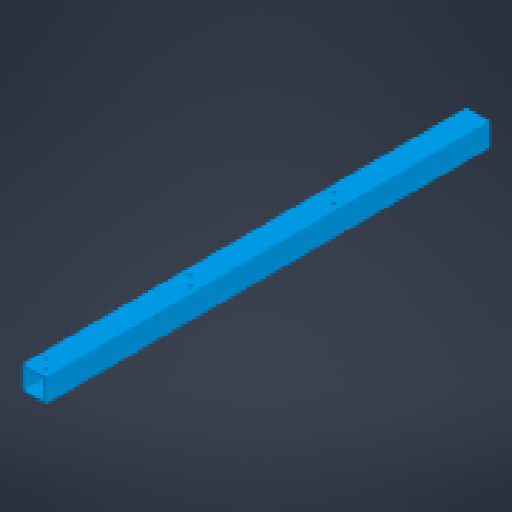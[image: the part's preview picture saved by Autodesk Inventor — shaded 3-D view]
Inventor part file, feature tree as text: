
AUTODESK INVENTOR PART (.ipt)
format: ipt  version: 2024 (Build 280153000, 153)  size: 178,176 bytes
history: native  units: mm
features: extrude x2, sketch x2, other x1
ambient origin geometry x8: Origin, YZ Plane, XZ Plane, XY Plane, X Axis, Y Axis, Z Axis, Center Point
bodies: Body1 (feature_tree)
feature tree (5):
  other  "Твердое тело1"
  extrude  "Выдавливание1"  Depth=380.0mm TaperAngle=0.0deg
  extrude  "Выдавливание3"  Depth=20.0mm
  sketch  "Эскиз1"
  sketch  "Эскиз6"
